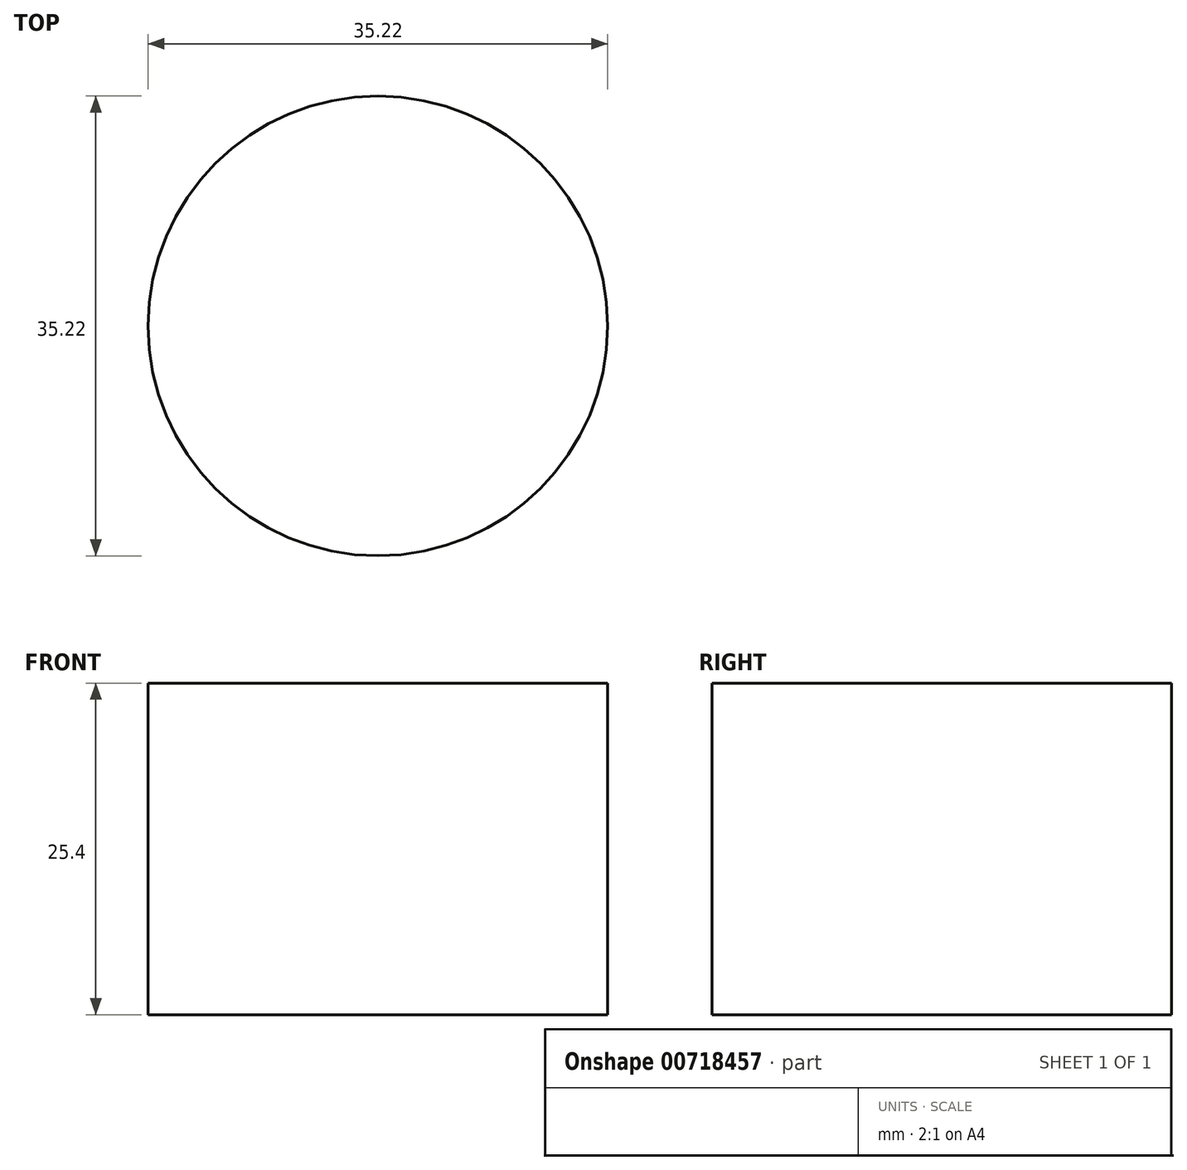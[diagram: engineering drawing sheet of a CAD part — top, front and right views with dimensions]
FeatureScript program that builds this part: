
annotation { "Feature Type Name" : "Feature", "Feature Type Description" : "" }
export const myFeature = defineFeature(function(context is Context, id is Id, definition is map)
    precondition{}
    {
        {
            var Q0;
            Q0=qCreatedBy(makeId("Top.planeOp"),FACE);
            var sketch = newSketch(context, id + "F0", { "sketchPlane" : qUnion([Q0])});
            skCircle(sketch, "E0", {"center": v(0, 0) * mm, "radius": 17.6 * mm});
            skSolve(sketch);
        }
        {
            var Q0;
            Q0 = qSketchRegion(id + "F0", true);
            extrude(context, id + "F1", {"entities" : qUnion([Q0]), "depth" : 25.4 * mm, "offsetDistance" : 25.4 * mm});
        }
    });
